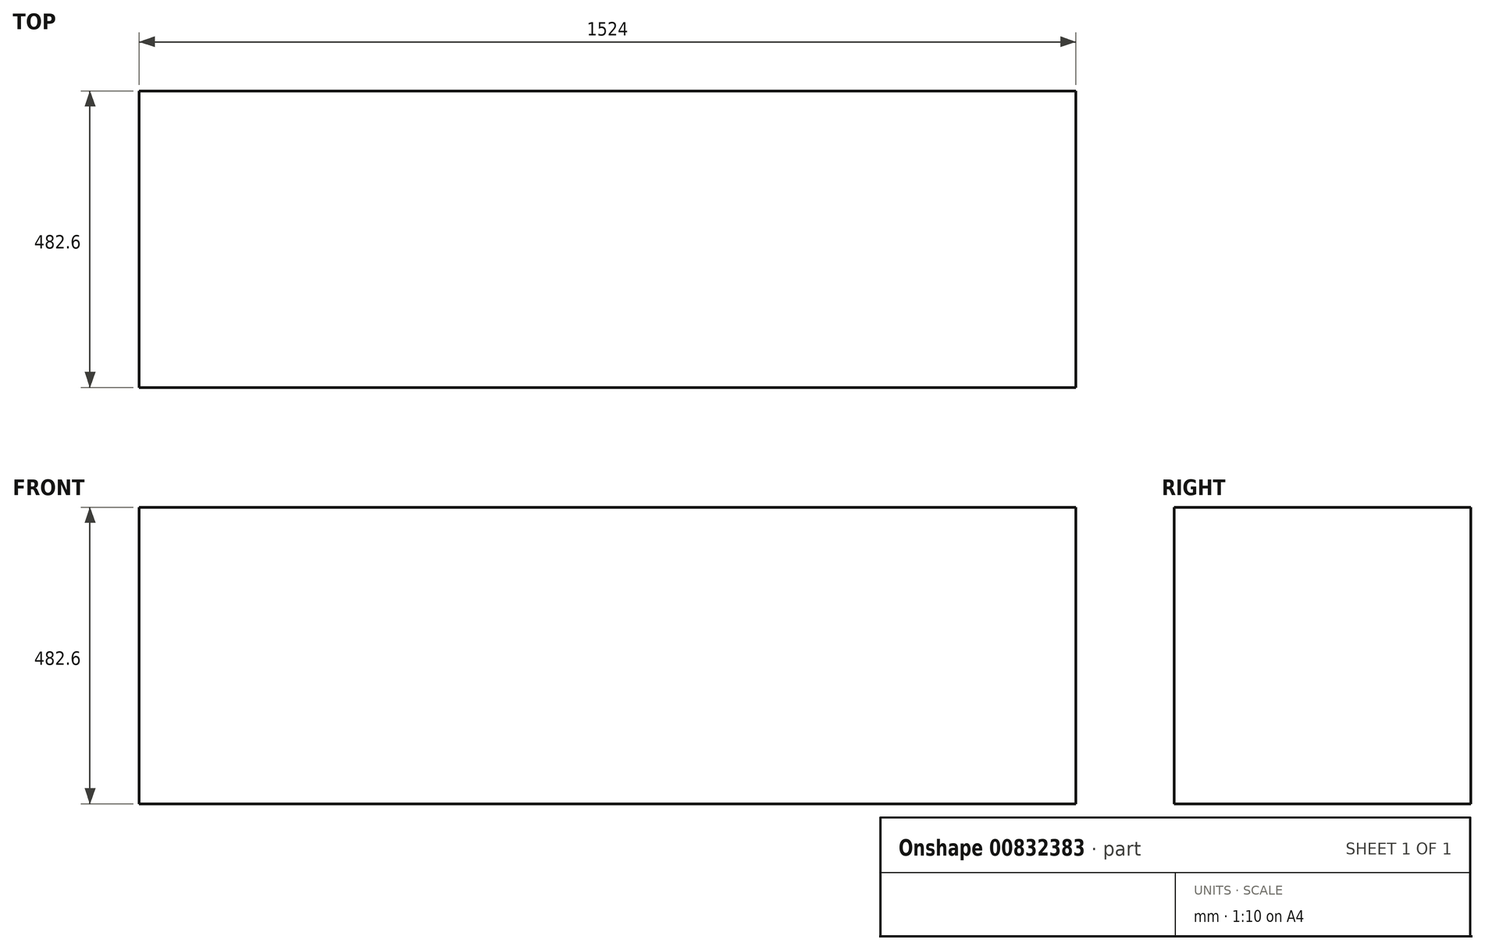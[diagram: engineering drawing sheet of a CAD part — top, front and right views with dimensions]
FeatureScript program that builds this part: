
annotation { "Feature Type Name" : "Feature", "Feature Type Description" : "" }
export const myFeature = defineFeature(function(context is Context, id is Id, definition is map)
    precondition{}
    {
        {
            var Q0;
            Q0=qCreatedBy(makeId("Front.planeOp"),FACE);
            var sketch = newSketch(context, id + "F0", { "sketchPlane" : qUnion([Q0])});
            skLineSegment(sketch, "E0.bottom", {"start": v(0, 0) * mm, "end": v(-1524, 0) * mm});
            skLineSegment(sketch, "E0.top", {"start": v(0, 482.6) * mm, "end": v(-1524, 482.6) * mm});
            skLineSegment(sketch, "E0.left", {"start": v(0, 0) * mm, "end": v(0, 482.6) * mm});
            skLineSegment(sketch, "E0.right", {"start": v(-1524, 0) * mm, "end": v(-1524, 482.6) * mm});
            skSolve(sketch);
        }
        {
            var Q0;
            Q0 = qSketchRegion(id + "F0", true);
            extrude(context, id + "F1", {"entities" : qUnion([Q0]), "endBound" : BoundingType.SYMMETRIC, "depth" : 482.6 * mm, "offsetDistance" : 25.4 * mm});
        }
    });
